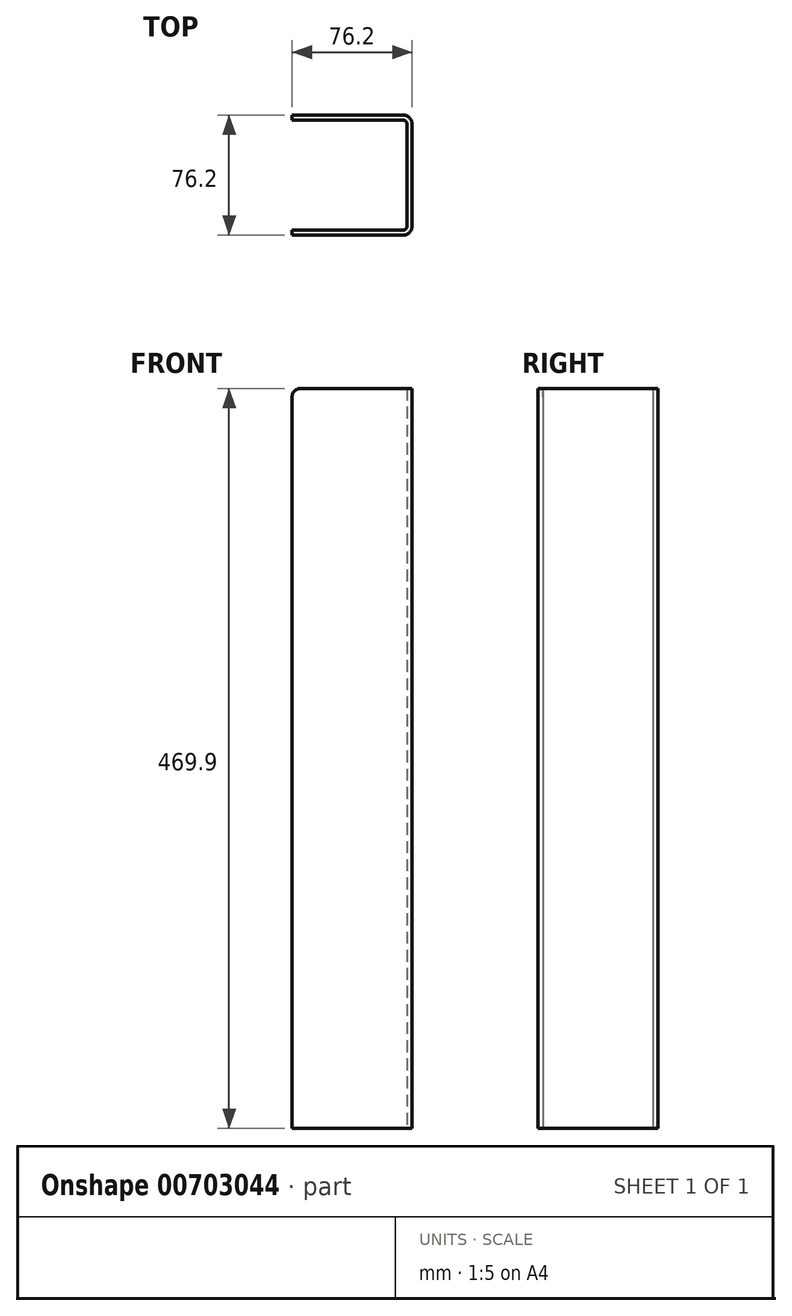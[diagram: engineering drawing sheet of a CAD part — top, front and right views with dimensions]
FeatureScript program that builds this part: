
annotation { "Feature Type Name" : "Feature", "Feature Type Description" : "" }
export const myFeature = defineFeature(function(context is Context, id is Id, definition is map)
    precondition{}
    {
        {
            var Q0;
            Q0=qCreatedBy(makeId("Top.planeOp"),FACE);
            var sketch = newSketch(context, id + "F0", { "sketchPlane" : qUnion([Q0])});
            skLineSegment(sketch, "E0", {"start": v(-76.2, 42.27) * mm, "end": v(-5.71, 42.27) * mm});
            skLineSegment(sketch, "E1", {"start": v(0, 36.55) * mm, "end": v(0, -28.22) * mm});
            skLineSegment(sketch, "E2", {"start": v(-5.71, -33.93) * mm, "end": v(-76.2, -33.93) * mm});
            skLineSegment(sketch, "E3", {"start": v(-76.2, -33.93) * mm, "end": v(-76.2, -30.76) * mm});
            skLineSegment(sketch, "E4", {"start": v(-76.2, -30.76) * mm, "end": v(-5.71, -30.76) * mm});
            skLineSegment(sketch, "E5", {"start": v(-3.17, -28.22) * mm, "end": v(-3.18, 36.55) * mm});
            skLineSegment(sketch, "E6", {"start": v(-5.71, 39.1) * mm, "end": v(-76.2, 39.1) * mm});
            skLineSegment(sketch, "E7", {"start": v(-76.2, 39.1) * mm, "end": v(-76.2, 42.27) * mm});
            skPoint(sketch, "E8.visualSharp", {"position": v(-3.18, 39.1) * mm});
            skArc(sketch, "E8.filletArc", {"start": v(-3.17, 36.55) * mm, "mid": v(-3.92, 38.35) * mm, "end": v(-5.71, 39.1) * mm});
            skPoint(sketch, "E9.visualSharp", {"position": v(-3.17, -30.76) * mm});
            skArc(sketch, "E9.filletArc", {"start": v(-5.71, -30.76) * mm, "mid": v(-3.92, -30.01) * mm, "end": v(-3.17, -28.22) * mm});
            skPoint(sketch, "E10.visualSharp", {"position": v(0, 42.27) * mm});
            skArc(sketch, "E10.filletArc", {"start": v(0, 36.55) * mm, "mid": v(-1.67, 40.6) * mm, "end": v(-5.71, 42.27) * mm});
            skPoint(sketch, "E11.visualSharp", {"position": v(0, -33.93) * mm});
            skArc(sketch, "E11.filletArc", {"start": v(-5.71, -33.93) * mm, "mid": v(-1.67, -32.26) * mm, "end": v(0, -28.22) * mm});
            skSolve(sketch);
        }
        {
            var Q0;
            Q0=makeQuery(id+"F0.imprint","IMPRINT",FACE,{"disambiguationData":[TD([[makeQuery(id+"F0.imprint","IMPRINT",EDGE,{"derivedFrom":sQuery(id+"F0.wireOp",EDGE,"E0")}),-1.0]])]});
            extrude(context, id + "F1", {"entities" : qUnion([Q0]), "depth" : 469.9 * mm, "offsetDistance" : 25.4 * mm});
        }
        {
            var Q0;
            Q0=makeQuery(id+"F1.opExtrude","CAP_EDGE",EDGE,{"disambiguationData":[OSD([sQuery(id+"F0.wireOp",EDGE,"E3")])],"isStart":false});
            var Q1;
            Q1=makeQuery(id+"F1.opExtrude","CAP_EDGE",EDGE,{"disambiguationData":[OSD([sQuery(id+"F0.wireOp",EDGE,"E7")])],"isStart":false});
            fillet(context, id + "F2", {"entities" : qUnion([Q0, Q1]), "radius" : 5.08 * mm, "tangentPropagation" : true, "allowEdgeOverflow" : false});
        }
    });
